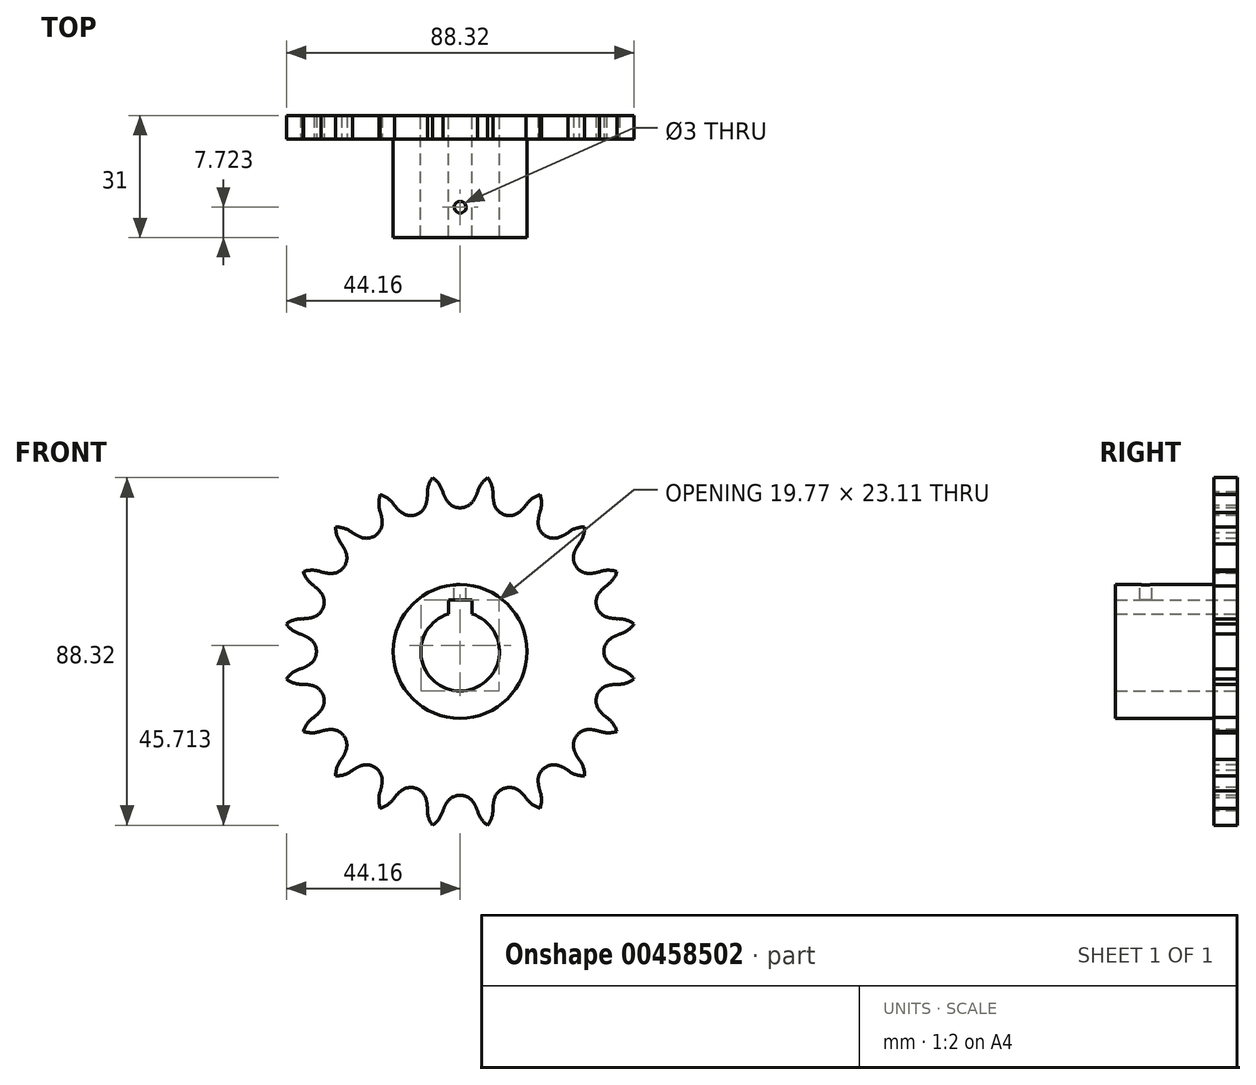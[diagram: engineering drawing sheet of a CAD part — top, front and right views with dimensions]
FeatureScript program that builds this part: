
annotation { "Feature Type Name" : "Feature", "Feature Type Description" : "" }
export const myFeature = defineFeature(function(context is Context, id is Id, definition is map)
    precondition{}
    {
        {
            var Q0;
            Q0=qCreatedBy(makeId("Front.planeOp"),FACE);
            var sketch = newSketch(context, id + "F0", { "sketchPlane" : qUnion([Q0])});
            skCircle(sketch, "E0", {"center": v(0, 0) * mm, "radius": 17 * mm});
            skArc(sketch, "E1", {"start": v(-3, 9.54) * mm, "mid": v(0, -10) * mm, "end": v(3, 9.54) * mm});
            skLineSegment(sketch, "E2", {"start": v(0, 13.1) * mm, "end": v(3, 13.1) * mm});
            skLineSegment(sketch, "E3", {"start": v(0, 13.1) * mm, "end": v(-3, 13.1) * mm});
            skLineSegment(sketch, "E4", {"start": v(-3, 13.1) * mm, "end": v(-3, 9.54) * mm});
            skLineSegment(sketch, "E5", {"start": v(3, 9.54) * mm, "end": v(3, 13.1) * mm});
            skSolve(sketch);
        }
        {
            var Q0;
            Q0=makeQuery(id+"F0.imprint","IMPRINT",FACE,{"disambiguationData":[TD([[makeQuery(id+"F0.imprint","IMPRINT",EDGE,{"derivedFrom":sQuery(id+"F0.wireOp",EDGE,"E0")}),1.0]])]});
            extrude(context, id + "F1", {"entities" : qUnion([Q0]), "depth" : 25 * mm, "offsetDistance" : 25 * mm});
        }
        {
            var Q0;
            Q0=qCreatedBy(makeId("Top.planeOp"),FACE);
            cPlane(context, id + "F2", {"entities" : qUnion([Q0]), "cplaneType" : CPlaneType.OFFSET, "offset" : 17 * mm, "width" : 150 * mm, "height" : 150 * mm});
        }
        {
            var Q0;
            Q0=qCreatedBy(id+"F2.planeOp",FACE);
            var sketch = newSketch(context, id + "F3", { "sketchPlane" : qUnion([Q0])});
            skLineSegment(sketch, "E6", {"start": v(0, -25.28) * mm, "end": v(0, -17.28) * mm, "construction": true});
            skCircle(sketch, "E7", {"center": v(0, -17.28) * mm, "radius": 1.5 * mm, "construction": true});
            skCircle(sketch, "E8", {"center": v(0, -17.28) * mm, "radius": 1.5 * mm});
            skSolve(sketch);
        }
        {
            var Q0;
            Q0=makeQuery(id+"F3.imprint","IMPRINT",FACE,{"disambiguationData":[TD([[makeQuery(id+"F3.imprint","IMPRINT",EDGE,{"derivedFrom":sQuery(id+"F3.wireOp",EDGE,"E8")}),1.0]])]});
            extrude(context, id + "F4", {"entities" : qUnion([Q0]), "operationType" : NewBodyOperationType.REMOVE, "oppositeDirection" : true, "depth" : 5.5 * mm, "offsetDistance" : 25 * mm});
        }
        {
            var Q0;
            Q0=qCreatedBy(makeId("Front.planeOp"),FACE);
            var sketch = newSketch(context, id + "F5", { "sketchPlane" : qUnion([Q0])});
            skCircle(sketch, "E9", {"center": v(0, 0) * mm, "radius": 40.5 * mm, "construction": true});
            skLineSegment(sketch, "E10", {"start": v(0, 40.5) * mm, "end": v(-50.2, 40.5) * mm, "construction": true});
            skLineSegment(sketch, "E11", {"start": v(-50.2, 40.5) * mm, "end": v(-50.2, 38.77) * mm, "construction": true});
            skLineSegment(sketch, "E12", {"start": v(0, 40.5) * mm, "end": v(0, 16.87) * mm, "construction": true});
            skLineSegment(sketch, "E13", {"start": v(0, 40.5) * mm, "end": v(55.48, 40.5) * mm, "construction": true});
            skLineSegment(sketch, "E14", {"start": v(0, 40.5) * mm, "end": v(5.34, 43.9) * mm, "construction": true});
            skLineSegment(sketch, "E15", {"start": v(5.34, 43.9) * mm, "end": v(-4.51, 40.84) * mm, "construction": true});
            skArc(sketch, "E16", {"start": v(-4.4, 40.5) * mm, "mid": v(-3.95, 39.4) * mm, "end": v(-3.37, 38.36) * mm});
            skArc(sketch, "E17", {"start": v(-4.4, 40.5) * mm, "mid": v(-5.38, 42.56) * mm, "end": v(-7, 44.16) * mm});
            skLineSegment(sketch, "E18", {"start": v(0, 0) * mm, "end": v(-9.88, 62.4) * mm, "construction": true});
            skArc(sketch, "E19.trimOffspring", {"start": v(-3.37, 38.36) * mm, "mid": v(-1.92, 37) * mm, "end": v(0, 36.51) * mm});
            skArc(sketch, "E20.MirrorCS", {"start": v(4.4, 40.5) * mm, "mid": v(5.38, 42.56) * mm, "end": v(7, 44.16) * mm});
            skArc(sketch, "E21.MirrorCS", {"start": v(4.4, 40.5) * mm, "mid": v(3.95, 39.4) * mm, "end": v(3.37, 38.36) * mm});
            skArc(sketch, "E22.MirrorCS", {"start": v(3.37, 38.36) * mm, "mid": v(1.92, 37) * mm, "end": v(0, 36.51) * mm});
            skArc(sketch, "E23.1.0", {"start": v(-16.7, 37.16) * mm, "mid": v(-18.27, 38.81) * mm, "end": v(-20.3, 39.84) * mm});
            skArc(sketch, "E23.1.1", {"start": v(-16.7, 37.16) * mm, "mid": v(-15.93, 36.25) * mm, "end": v(-15.06, 35.44) * mm});
            skArc(sketch, "E23.1.2", {"start": v(-15.06, 35.44) * mm, "mid": v(-13.26, 34.6) * mm, "end": v(-11.28, 34.73) * mm});
            skArc(sketch, "E23.1.3", {"start": v(-8.65, 37.52) * mm, "mid": v(-9.6, 35.79) * mm, "end": v(-11.28, 34.73) * mm});
            skArc(sketch, "E23.1.4", {"start": v(-8.33, 39.88) * mm, "mid": v(-8.42, 38.7) * mm, "end": v(-8.65, 37.52) * mm});
            skArc(sketch, "E23.1.5", {"start": v(-8.33, 39.88) * mm, "mid": v(-8.04, 42.14) * mm, "end": v(-7, 44.16) * mm});
            skArc(sketch, "E23.2.0", {"start": v(-27.37, 30.18) * mm, "mid": v(-29.36, 31.27) * mm, "end": v(-31.61, 31.61) * mm});
            skArc(sketch, "E23.2.1", {"start": v(-27.37, 30.18) * mm, "mid": v(-26.35, 29.55) * mm, "end": v(-25.27, 29.05) * mm});
            skArc(sketch, "E23.2.2", {"start": v(-25.27, 29.05) * mm, "mid": v(-23.3, 28.8) * mm, "end": v(-21.46, 29.54) * mm});
            skArc(sketch, "E23.2.3", {"start": v(-19.82, 33.01) * mm, "mid": v(-20.2, 31.07) * mm, "end": v(-21.46, 29.54) * mm});
            skArc(sketch, "E23.2.4", {"start": v(-20.24, 35.35) * mm, "mid": v(-19.96, 34.2) * mm, "end": v(-19.82, 33.01) * mm});
            skArc(sketch, "E23.2.5", {"start": v(-20.24, 35.35) * mm, "mid": v(-20.66, 37.6) * mm, "end": v(-20.3, 39.84) * mm});
            skArc(sketch, "E23.3.0", {"start": v(-35.35, 20.24) * mm, "mid": v(-37.6, 20.66) * mm, "end": v(-39.84, 20.3) * mm});
            skArc(sketch, "E23.3.1", {"start": v(-35.35, 20.24) * mm, "mid": v(-34.2, 19.96) * mm, "end": v(-33.01, 19.82) * mm});
            skArc(sketch, "E23.3.2", {"start": v(-33.01, 19.82) * mm, "mid": v(-31.07, 20.2) * mm, "end": v(-29.54, 21.46) * mm});
            skArc(sketch, "E23.3.3", {"start": v(-29.05, 25.27) * mm, "mid": v(-28.8, 23.3) * mm, "end": v(-29.54, 21.46) * mm});
            skArc(sketch, "E23.3.4", {"start": v(-30.18, 27.37) * mm, "mid": v(-29.55, 26.35) * mm, "end": v(-29.05, 25.27) * mm});
            skArc(sketch, "E23.3.5", {"start": v(-30.18, 27.37) * mm, "mid": v(-31.27, 29.36) * mm, "end": v(-31.61, 31.61) * mm});
            skArc(sketch, "E23.4.0", {"start": v(-39.88, 8.33) * mm, "mid": v(-42.14, 8.04) * mm, "end": v(-44.16, 7) * mm});
            skArc(sketch, "E23.4.1", {"start": v(-39.88, 8.33) * mm, "mid": v(-38.7, 8.42) * mm, "end": v(-37.52, 8.65) * mm});
            skArc(sketch, "E23.4.2", {"start": v(-37.52, 8.65) * mm, "mid": v(-35.79, 9.6) * mm, "end": v(-34.73, 11.28) * mm});
            skArc(sketch, "E23.4.3", {"start": v(-35.44, 15.06) * mm, "mid": v(-34.6, 13.26) * mm, "end": v(-34.73, 11.28) * mm});
            skArc(sketch, "E23.4.4", {"start": v(-37.16, 16.7) * mm, "mid": v(-36.25, 15.93) * mm, "end": v(-35.44, 15.06) * mm});
            skArc(sketch, "E23.4.5", {"start": v(-37.16, 16.7) * mm, "mid": v(-38.81, 18.27) * mm, "end": v(-39.84, 20.3) * mm});
            skArc(sketch, "E23.5.0", {"start": v(-40.5, -4.4) * mm, "mid": v(-42.56, -5.38) * mm, "end": v(-44.16, -7) * mm});
            skArc(sketch, "E23.5.1", {"start": v(-40.5, -4.4) * mm, "mid": v(-39.4, -3.95) * mm, "end": v(-38.36, -3.37) * mm});
            skArc(sketch, "E23.5.2", {"start": v(-38.36, -3.37) * mm, "mid": v(-37, -1.92) * mm, "end": v(-36.51, 0) * mm});
            skArc(sketch, "E23.5.3", {"start": v(-38.36, 3.37) * mm, "mid": v(-37, 1.92) * mm, "end": v(-36.51, 0) * mm});
            skArc(sketch, "E23.5.4", {"start": v(-40.5, 4.4) * mm, "mid": v(-39.4, 3.95) * mm, "end": v(-38.36, 3.37) * mm});
            skArc(sketch, "E23.5.5", {"start": v(-40.5, 4.4) * mm, "mid": v(-42.56, 5.38) * mm, "end": v(-44.16, 7) * mm});
            skArc(sketch, "E23.6.0", {"start": v(-37.16, -16.7) * mm, "mid": v(-38.81, -18.27) * mm, "end": v(-39.84, -20.3) * mm});
            skArc(sketch, "E23.6.1", {"start": v(-37.16, -16.7) * mm, "mid": v(-36.25, -15.93) * mm, "end": v(-35.44, -15.06) * mm});
            skArc(sketch, "E23.6.2", {"start": v(-35.44, -15.06) * mm, "mid": v(-34.6, -13.26) * mm, "end": v(-34.73, -11.28) * mm});
            skArc(sketch, "E23.6.3", {"start": v(-37.52, -8.65) * mm, "mid": v(-35.79, -9.6) * mm, "end": v(-34.73, -11.28) * mm});
            skArc(sketch, "E23.6.4", {"start": v(-39.88, -8.33) * mm, "mid": v(-38.7, -8.42) * mm, "end": v(-37.52, -8.65) * mm});
            skArc(sketch, "E23.6.5", {"start": v(-39.88, -8.33) * mm, "mid": v(-42.14, -8.04) * mm, "end": v(-44.16, -7) * mm});
            skArc(sketch, "E23.7.0", {"start": v(-30.18, -27.37) * mm, "mid": v(-31.27, -29.36) * mm, "end": v(-31.61, -31.61) * mm});
            skArc(sketch, "E23.7.1", {"start": v(-30.18, -27.37) * mm, "mid": v(-29.55, -26.35) * mm, "end": v(-29.05, -25.27) * mm});
            skArc(sketch, "E23.7.2", {"start": v(-29.05, -25.27) * mm, "mid": v(-28.8, -23.3) * mm, "end": v(-29.54, -21.46) * mm});
            skArc(sketch, "E23.7.3", {"start": v(-33.01, -19.82) * mm, "mid": v(-31.07, -20.2) * mm, "end": v(-29.54, -21.46) * mm});
            skArc(sketch, "E23.7.4", {"start": v(-35.35, -20.24) * mm, "mid": v(-34.2, -19.96) * mm, "end": v(-33.01, -19.82) * mm});
            skArc(sketch, "E23.7.5", {"start": v(-35.35, -20.24) * mm, "mid": v(-37.6, -20.66) * mm, "end": v(-39.84, -20.3) * mm});
            skArc(sketch, "E23.8.0", {"start": v(-20.24, -35.35) * mm, "mid": v(-20.66, -37.6) * mm, "end": v(-20.3, -39.84) * mm});
            skArc(sketch, "E23.8.1", {"start": v(-20.24, -35.35) * mm, "mid": v(-19.96, -34.2) * mm, "end": v(-19.82, -33.01) * mm});
            skArc(sketch, "E23.8.2", {"start": v(-19.82, -33.01) * mm, "mid": v(-20.2, -31.07) * mm, "end": v(-21.46, -29.54) * mm});
            skArc(sketch, "E23.8.3", {"start": v(-25.27, -29.05) * mm, "mid": v(-23.3, -28.8) * mm, "end": v(-21.46, -29.54) * mm});
            skArc(sketch, "E23.8.4", {"start": v(-27.37, -30.18) * mm, "mid": v(-26.35, -29.55) * mm, "end": v(-25.27, -29.05) * mm});
            skArc(sketch, "E23.8.5", {"start": v(-27.37, -30.18) * mm, "mid": v(-29.36, -31.27) * mm, "end": v(-31.61, -31.61) * mm});
            skArc(sketch, "E23.9.0", {"start": v(-8.33, -39.88) * mm, "mid": v(-8.04, -42.14) * mm, "end": v(-7, -44.16) * mm});
            skArc(sketch, "E23.9.1", {"start": v(-8.33, -39.88) * mm, "mid": v(-8.42, -38.7) * mm, "end": v(-8.65, -37.52) * mm});
            skArc(sketch, "E23.9.2", {"start": v(-8.65, -37.52) * mm, "mid": v(-9.6, -35.79) * mm, "end": v(-11.28, -34.73) * mm});
            skArc(sketch, "E23.9.3", {"start": v(-15.06, -35.44) * mm, "mid": v(-13.26, -34.6) * mm, "end": v(-11.28, -34.73) * mm});
            skArc(sketch, "E23.9.4", {"start": v(-16.7, -37.16) * mm, "mid": v(-15.93, -36.25) * mm, "end": v(-15.06, -35.44) * mm});
            skArc(sketch, "E23.9.5", {"start": v(-16.7, -37.16) * mm, "mid": v(-18.27, -38.81) * mm, "end": v(-20.3, -39.84) * mm});
            skArc(sketch, "E23.10.0", {"start": v(4.4, -40.5) * mm, "mid": v(5.38, -42.56) * mm, "end": v(7, -44.16) * mm});
            skArc(sketch, "E23.10.1", {"start": v(4.4, -40.5) * mm, "mid": v(3.95, -39.4) * mm, "end": v(3.37, -38.36) * mm});
            skArc(sketch, "E23.10.2", {"start": v(3.37, -38.36) * mm, "mid": v(1.92, -37) * mm, "end": v(0, -36.51) * mm});
            skArc(sketch, "E23.10.3", {"start": v(-3.37, -38.36) * mm, "mid": v(-1.92, -37) * mm, "end": v(0, -36.51) * mm});
            skArc(sketch, "E23.10.4", {"start": v(-4.4, -40.5) * mm, "mid": v(-3.95, -39.4) * mm, "end": v(-3.37, -38.36) * mm});
            skArc(sketch, "E23.10.5", {"start": v(-4.4, -40.5) * mm, "mid": v(-5.38, -42.56) * mm, "end": v(-7, -44.16) * mm});
            skArc(sketch, "E23.11.0", {"start": v(16.7, -37.16) * mm, "mid": v(18.27, -38.81) * mm, "end": v(20.3, -39.84) * mm});
            skArc(sketch, "E23.11.1", {"start": v(16.7, -37.16) * mm, "mid": v(15.93, -36.25) * mm, "end": v(15.06, -35.44) * mm});
            skArc(sketch, "E23.11.2", {"start": v(15.06, -35.44) * mm, "mid": v(13.26, -34.6) * mm, "end": v(11.28, -34.73) * mm});
            skArc(sketch, "E23.11.3", {"start": v(8.65, -37.52) * mm, "mid": v(9.6, -35.79) * mm, "end": v(11.28, -34.73) * mm});
            skArc(sketch, "E23.11.4", {"start": v(8.33, -39.88) * mm, "mid": v(8.42, -38.7) * mm, "end": v(8.65, -37.52) * mm});
            skArc(sketch, "E23.11.5", {"start": v(8.33, -39.88) * mm, "mid": v(8.04, -42.14) * mm, "end": v(7, -44.16) * mm});
            skArc(sketch, "E23.12.0", {"start": v(27.37, -30.18) * mm, "mid": v(29.36, -31.27) * mm, "end": v(31.61, -31.61) * mm});
            skArc(sketch, "E23.12.1", {"start": v(27.37, -30.18) * mm, "mid": v(26.35, -29.55) * mm, "end": v(25.27, -29.05) * mm});
            skArc(sketch, "E23.12.2", {"start": v(25.27, -29.05) * mm, "mid": v(23.3, -28.8) * mm, "end": v(21.46, -29.54) * mm});
            skArc(sketch, "E23.12.3", {"start": v(19.82, -33.01) * mm, "mid": v(20.2, -31.07) * mm, "end": v(21.46, -29.54) * mm});
            skArc(sketch, "E23.12.4", {"start": v(20.24, -35.35) * mm, "mid": v(19.96, -34.2) * mm, "end": v(19.82, -33.01) * mm});
            skArc(sketch, "E23.12.5", {"start": v(20.24, -35.35) * mm, "mid": v(20.66, -37.6) * mm, "end": v(20.3, -39.84) * mm});
            skArc(sketch, "E23.13.0", {"start": v(35.35, -20.24) * mm, "mid": v(37.6, -20.66) * mm, "end": v(39.84, -20.3) * mm});
            skArc(sketch, "E23.13.1", {"start": v(35.35, -20.24) * mm, "mid": v(34.2, -19.96) * mm, "end": v(33.01, -19.82) * mm});
            skArc(sketch, "E23.13.2", {"start": v(33.01, -19.82) * mm, "mid": v(31.07, -20.2) * mm, "end": v(29.54, -21.46) * mm});
            skArc(sketch, "E23.13.3", {"start": v(29.05, -25.27) * mm, "mid": v(28.8, -23.3) * mm, "end": v(29.54, -21.46) * mm});
            skArc(sketch, "E23.13.4", {"start": v(30.18, -27.37) * mm, "mid": v(29.55, -26.35) * mm, "end": v(29.05, -25.27) * mm});
            skArc(sketch, "E23.13.5", {"start": v(30.18, -27.37) * mm, "mid": v(31.27, -29.36) * mm, "end": v(31.61, -31.61) * mm});
            skArc(sketch, "E23.14.0", {"start": v(39.88, -8.33) * mm, "mid": v(42.14, -8.04) * mm, "end": v(44.16, -7) * mm});
            skArc(sketch, "E23.14.1", {"start": v(39.88, -8.33) * mm, "mid": v(38.7, -8.42) * mm, "end": v(37.52, -8.65) * mm});
            skArc(sketch, "E23.14.2", {"start": v(37.52, -8.65) * mm, "mid": v(35.79, -9.6) * mm, "end": v(34.73, -11.28) * mm});
            skArc(sketch, "E23.14.3", {"start": v(35.44, -15.06) * mm, "mid": v(34.6, -13.26) * mm, "end": v(34.73, -11.28) * mm});
            skArc(sketch, "E23.14.4", {"start": v(37.16, -16.7) * mm, "mid": v(36.25, -15.93) * mm, "end": v(35.44, -15.06) * mm});
            skArc(sketch, "E23.14.5", {"start": v(37.16, -16.7) * mm, "mid": v(38.81, -18.27) * mm, "end": v(39.84, -20.3) * mm});
            skArc(sketch, "E23.15.0", {"start": v(40.5, 4.4) * mm, "mid": v(42.56, 5.38) * mm, "end": v(44.16, 7) * mm});
            skArc(sketch, "E23.15.1", {"start": v(40.5, 4.4) * mm, "mid": v(39.4, 3.95) * mm, "end": v(38.36, 3.37) * mm});
            skArc(sketch, "E23.15.2", {"start": v(38.36, 3.37) * mm, "mid": v(37, 1.92) * mm, "end": v(36.51, 0) * mm});
            skArc(sketch, "E23.15.3", {"start": v(38.36, -3.37) * mm, "mid": v(37, -1.92) * mm, "end": v(36.51, 0) * mm});
            skArc(sketch, "E23.15.4", {"start": v(40.5, -4.4) * mm, "mid": v(39.4, -3.95) * mm, "end": v(38.36, -3.37) * mm});
            skArc(sketch, "E23.15.5", {"start": v(40.5, -4.4) * mm, "mid": v(42.56, -5.38) * mm, "end": v(44.16, -7) * mm});
            skArc(sketch, "E23.16.0", {"start": v(37.16, 16.7) * mm, "mid": v(38.81, 18.27) * mm, "end": v(39.84, 20.3) * mm});
            skArc(sketch, "E23.16.1", {"start": v(37.16, 16.7) * mm, "mid": v(36.25, 15.93) * mm, "end": v(35.44, 15.06) * mm});
            skArc(sketch, "E23.16.2", {"start": v(35.44, 15.06) * mm, "mid": v(34.6, 13.26) * mm, "end": v(34.73, 11.28) * mm});
            skArc(sketch, "E23.16.3", {"start": v(37.52, 8.65) * mm, "mid": v(35.79, 9.6) * mm, "end": v(34.73, 11.28) * mm});
            skArc(sketch, "E23.16.4", {"start": v(39.88, 8.33) * mm, "mid": v(38.7, 8.42) * mm, "end": v(37.52, 8.65) * mm});
            skArc(sketch, "E23.16.5", {"start": v(39.88, 8.33) * mm, "mid": v(42.14, 8.04) * mm, "end": v(44.16, 7) * mm});
            skArc(sketch, "E23.17.0", {"start": v(30.18, 27.37) * mm, "mid": v(31.27, 29.36) * mm, "end": v(31.61, 31.61) * mm});
            skArc(sketch, "E23.17.1", {"start": v(30.18, 27.37) * mm, "mid": v(29.55, 26.35) * mm, "end": v(29.05, 25.27) * mm});
            skArc(sketch, "E23.17.2", {"start": v(29.05, 25.27) * mm, "mid": v(28.8, 23.3) * mm, "end": v(29.54, 21.46) * mm});
            skArc(sketch, "E23.17.3", {"start": v(33.01, 19.82) * mm, "mid": v(31.07, 20.2) * mm, "end": v(29.54, 21.46) * mm});
            skArc(sketch, "E23.17.4", {"start": v(35.35, 20.24) * mm, "mid": v(34.2, 19.96) * mm, "end": v(33.01, 19.82) * mm});
            skArc(sketch, "E23.17.5", {"start": v(35.35, 20.24) * mm, "mid": v(37.6, 20.66) * mm, "end": v(39.84, 20.3) * mm});
            skArc(sketch, "E23.18.0", {"start": v(20.24, 35.35) * mm, "mid": v(20.66, 37.6) * mm, "end": v(20.3, 39.84) * mm});
            skArc(sketch, "E23.18.1", {"start": v(20.24, 35.35) * mm, "mid": v(19.96, 34.2) * mm, "end": v(19.82, 33.01) * mm});
            skArc(sketch, "E23.18.2", {"start": v(19.82, 33.01) * mm, "mid": v(20.2, 31.07) * mm, "end": v(21.46, 29.54) * mm});
            skArc(sketch, "E23.18.3", {"start": v(25.27, 29.05) * mm, "mid": v(23.3, 28.8) * mm, "end": v(21.46, 29.54) * mm});
            skArc(sketch, "E23.18.4", {"start": v(27.37, 30.18) * mm, "mid": v(26.35, 29.55) * mm, "end": v(25.27, 29.05) * mm});
            skArc(sketch, "E23.18.5", {"start": v(27.37, 30.18) * mm, "mid": v(29.36, 31.27) * mm, "end": v(31.61, 31.61) * mm});
            skArc(sketch, "E23.19.0", {"start": v(8.33, 39.88) * mm, "mid": v(8.04, 42.14) * mm, "end": v(7, 44.16) * mm});
            skArc(sketch, "E23.19.1", {"start": v(8.33, 39.88) * mm, "mid": v(8.42, 38.7) * mm, "end": v(8.65, 37.52) * mm});
            skArc(sketch, "E23.19.2", {"start": v(8.65, 37.52) * mm, "mid": v(9.6, 35.79) * mm, "end": v(11.28, 34.73) * mm});
            skArc(sketch, "E23.19.3", {"start": v(15.06, 35.44) * mm, "mid": v(13.26, 34.6) * mm, "end": v(11.28, 34.73) * mm});
            skArc(sketch, "E23.19.4", {"start": v(16.7, 37.16) * mm, "mid": v(15.93, 36.25) * mm, "end": v(15.06, 35.44) * mm});
            skArc(sketch, "E23.19.5", {"start": v(16.7, 37.16) * mm, "mid": v(18.27, 38.81) * mm, "end": v(20.3, 39.84) * mm});
            skSolve(sketch);
        }
        {
            var Q0;
            Q0=makeQuery(id+"F5.imprint","IMPRINT",FACE,{"disambiguationData":[TD([[makeQuery(id+"F5.imprint","IMPRINT",EDGE,{"derivedFrom":sQuery(id+"F5.wireOp",EDGE,"E16")}),-1.0]])]});
            extrude(context, id + "F6", {"entities" : qUnion([Q0]), "operationType" : NewBodyOperationType.ADD, "oppositeDirection" : true, "depth" : 6 * mm, "offsetDistance" : 25 * mm});
        }
        {
            var Q0;
            Q0=makeQuery(id+"F6.boolean.opBoolean","SPLIT",FACE,{"disambiguationData":[TD([makeQuery(id+"F1.opExtrude","SWEPT_FACE",FACE,{"disambiguationData":[OSD([sQuery(id+"F0.wireOp",EDGE,"E1")])]})])],"derivedFrom":makeQuery(id+"F6.opExtrude","CAP_FACE",FACE,{"disambiguationData":[OSD([sQuery(id+"F5.wireOp",EDGE,"E16"),sQuery(id+"F5.wireOp",EDGE,"E17"),sQuery(id+"F5.wireOp",EDGE,"E19.trimOffspring"),sQuery(id+"F5.wireOp",EDGE,"E20.MirrorCS"),sQuery(id+"F5.wireOp",EDGE,"E21.MirrorCS"),sQuery(id+"F5.wireOp",EDGE,"E22.MirrorCS"),sQuery(id+"F5.wireOp",EDGE,"E23.1.0"),sQuery(id+"F5.wireOp",EDGE,"E23.1.1"),sQuery(id+"F5.wireOp",EDGE,"E23.1.2"),sQuery(id+"F5.wireOp",EDGE,"E23.1.3"),sQuery(id+"F5.wireOp",EDGE,"E23.1.4"),sQuery(id+"F5.wireOp",EDGE,"E23.1.5"),sQuery(id+"F5.wireOp",EDGE,"E23.2.0"),sQuery(id+"F5.wireOp",EDGE,"E23.2.1"),sQuery(id+"F5.wireOp",EDGE,"E23.2.2"),sQuery(id+"F5.wireOp",EDGE,"E23.2.3"),sQuery(id+"F5.wireOp",EDGE,"E23.2.4"),sQuery(id+"F5.wireOp",EDGE,"E23.2.5"),sQuery(id+"F5.wireOp",EDGE,"E23.3.0"),sQuery(id+"F5.wireOp",EDGE,"E23.3.1"),sQuery(id+"F5.wireOp",EDGE,"E23.3.2"),sQuery(id+"F5.wireOp",EDGE,"E23.3.3"),sQuery(id+"F5.wireOp",EDGE,"E23.3.4"),sQuery(id+"F5.wireOp",EDGE,"E23.3.5"),sQuery(id+"F5.wireOp",EDGE,"E23.4.0"),sQuery(id+"F5.wireOp",EDGE,"E23.4.1"),sQuery(id+"F5.wireOp",EDGE,"E23.4.2"),sQuery(id+"F5.wireOp",EDGE,"E23.4.3"),sQuery(id+"F5.wireOp",EDGE,"E23.4.4"),sQuery(id+"F5.wireOp",EDGE,"E23.4.5"),sQuery(id+"F5.wireOp",EDGE,"E23.5.0"),sQuery(id+"F5.wireOp",EDGE,"E23.5.1"),sQuery(id+"F5.wireOp",EDGE,"E23.5.2"),sQuery(id+"F5.wireOp",EDGE,"E23.5.3"),sQuery(id+"F5.wireOp",EDGE,"E23.5.4"),sQuery(id+"F5.wireOp",EDGE,"E23.5.5"),sQuery(id+"F5.wireOp",EDGE,"E23.6.0"),sQuery(id+"F5.wireOp",EDGE,"E23.6.1"),sQuery(id+"F5.wireOp",EDGE,"E23.6.2"),sQuery(id+"F5.wireOp",EDGE,"E23.6.3"),sQuery(id+"F5.wireOp",EDGE,"E23.6.4"),sQuery(id+"F5.wireOp",EDGE,"E23.6.5"),sQuery(id+"F5.wireOp",EDGE,"E23.7.0"),sQuery(id+"F5.wireOp",EDGE,"E23.7.1"),sQuery(id+"F5.wireOp",EDGE,"E23.7.2"),sQuery(id+"F5.wireOp",EDGE,"E23.7.3"),sQuery(id+"F5.wireOp",EDGE,"E23.7.4"),sQuery(id+"F5.wireOp",EDGE,"E23.7.5"),sQuery(id+"F5.wireOp",EDGE,"E23.8.0"),sQuery(id+"F5.wireOp",EDGE,"E23.8.1"),sQuery(id+"F5.wireOp",EDGE,"E23.8.2"),sQuery(id+"F5.wireOp",EDGE,"E23.8.3"),sQuery(id+"F5.wireOp",EDGE,"E23.8.4"),sQuery(id+"F5.wireOp",EDGE,"E23.8.5"),sQuery(id+"F5.wireOp",EDGE,"E23.9.0"),sQuery(id+"F5.wireOp",EDGE,"E23.9.1"),sQuery(id+"F5.wireOp",EDGE,"E23.9.2"),sQuery(id+"F5.wireOp",EDGE,"E23.9.3"),sQuery(id+"F5.wireOp",EDGE,"E23.9.4"),sQuery(id+"F5.wireOp",EDGE,"E23.9.5"),sQuery(id+"F5.wireOp",EDGE,"E23.10.0"),sQuery(id+"F5.wireOp",EDGE,"E23.10.1"),sQuery(id+"F5.wireOp",EDGE,"E23.10.2"),sQuery(id+"F5.wireOp",EDGE,"E23.10.3"),sQuery(id+"F5.wireOp",EDGE,"E23.10.4"),sQuery(id+"F5.wireOp",EDGE,"E23.10.5"),sQuery(id+"F5.wireOp",EDGE,"E23.11.0"),sQuery(id+"F5.wireOp",EDGE,"E23.11.1"),sQuery(id+"F5.wireOp",EDGE,"E23.11.2"),sQuery(id+"F5.wireOp",EDGE,"E23.11.3"),sQuery(id+"F5.wireOp",EDGE,"E23.11.4"),sQuery(id+"F5.wireOp",EDGE,"E23.11.5"),sQuery(id+"F5.wireOp",EDGE,"E23.12.0"),sQuery(id+"F5.wireOp",EDGE,"E23.12.1"),sQuery(id+"F5.wireOp",EDGE,"E23.12.2"),sQuery(id+"F5.wireOp",EDGE,"E23.12.3"),sQuery(id+"F5.wireOp",EDGE,"E23.12.4"),sQuery(id+"F5.wireOp",EDGE,"E23.12.5"),sQuery(id+"F5.wireOp",EDGE,"E23.13.0"),sQuery(id+"F5.wireOp",EDGE,"E23.13.1"),sQuery(id+"F5.wireOp",EDGE,"E23.13.2"),sQuery(id+"F5.wireOp",EDGE,"E23.13.3"),sQuery(id+"F5.wireOp",EDGE,"E23.13.4"),sQuery(id+"F5.wireOp",EDGE,"E23.13.5"),sQuery(id+"F5.wireOp",EDGE,"E23.14.0"),sQuery(id+"F5.wireOp",EDGE,"E23.14.1"),sQuery(id+"F5.wireOp",EDGE,"E23.14.2"),sQuery(id+"F5.wireOp",EDGE,"E23.14.3"),sQuery(id+"F5.wireOp",EDGE,"E23.14.4"),sQuery(id+"F5.wireOp",EDGE,"E23.14.5"),sQuery(id+"F5.wireOp",EDGE,"E23.15.0"),sQuery(id+"F5.wireOp",EDGE,"E23.15.1"),sQuery(id+"F5.wireOp",EDGE,"E23.15.2"),sQuery(id+"F5.wireOp",EDGE,"E23.15.3"),sQuery(id+"F5.wireOp",EDGE,"E23.15.4"),sQuery(id+"F5.wireOp",EDGE,"E23.15.5"),sQuery(id+"F5.wireOp",EDGE,"E23.16.0"),sQuery(id+"F5.wireOp",EDGE,"E23.16.1"),sQuery(id+"F5.wireOp",EDGE,"E23.16.2"),sQuery(id+"F5.wireOp",EDGE,"E23.16.3"),sQuery(id+"F5.wireOp",EDGE,"E23.16.4"),sQuery(id+"F5.wireOp",EDGE,"E23.16.5"),sQuery(id+"F5.wireOp",EDGE,"E23.17.0"),sQuery(id+"F5.wireOp",EDGE,"E23.17.1"),sQuery(id+"F5.wireOp",EDGE,"E23.17.2"),sQuery(id+"F5.wireOp",EDGE,"E23.17.3"),sQuery(id+"F5.wireOp",EDGE,"E23.17.4"),sQuery(id+"F5.wireOp",EDGE,"E23.17.5"),sQuery(id+"F5.wireOp",EDGE,"E23.18.0"),sQuery(id+"F5.wireOp",EDGE,"E23.18.1"),sQuery(id+"F5.wireOp",EDGE,"E23.18.2"),sQuery(id+"F5.wireOp",EDGE,"E23.18.3"),sQuery(id+"F5.wireOp",EDGE,"E23.18.4"),sQuery(id+"F5.wireOp",EDGE,"E23.18.5"),sQuery(id+"F5.wireOp",EDGE,"E23.19.0"),sQuery(id+"F5.wireOp",EDGE,"E23.19.1"),sQuery(id+"F5.wireOp",EDGE,"E23.19.2"),sQuery(id+"F5.wireOp",EDGE,"E23.19.3"),sQuery(id+"F5.wireOp",EDGE,"E23.19.4"),sQuery(id+"F5.wireOp",EDGE,"E23.19.5")])],"isStart":true})});
            extrude(context, id + "F7", {"entities" : qUnion([Q0]), "operationType" : NewBodyOperationType.REMOVE, "oppositeDirection" : true, "depth" : 25 * mm, "offsetDistance" : 25 * mm});
        }
    });
